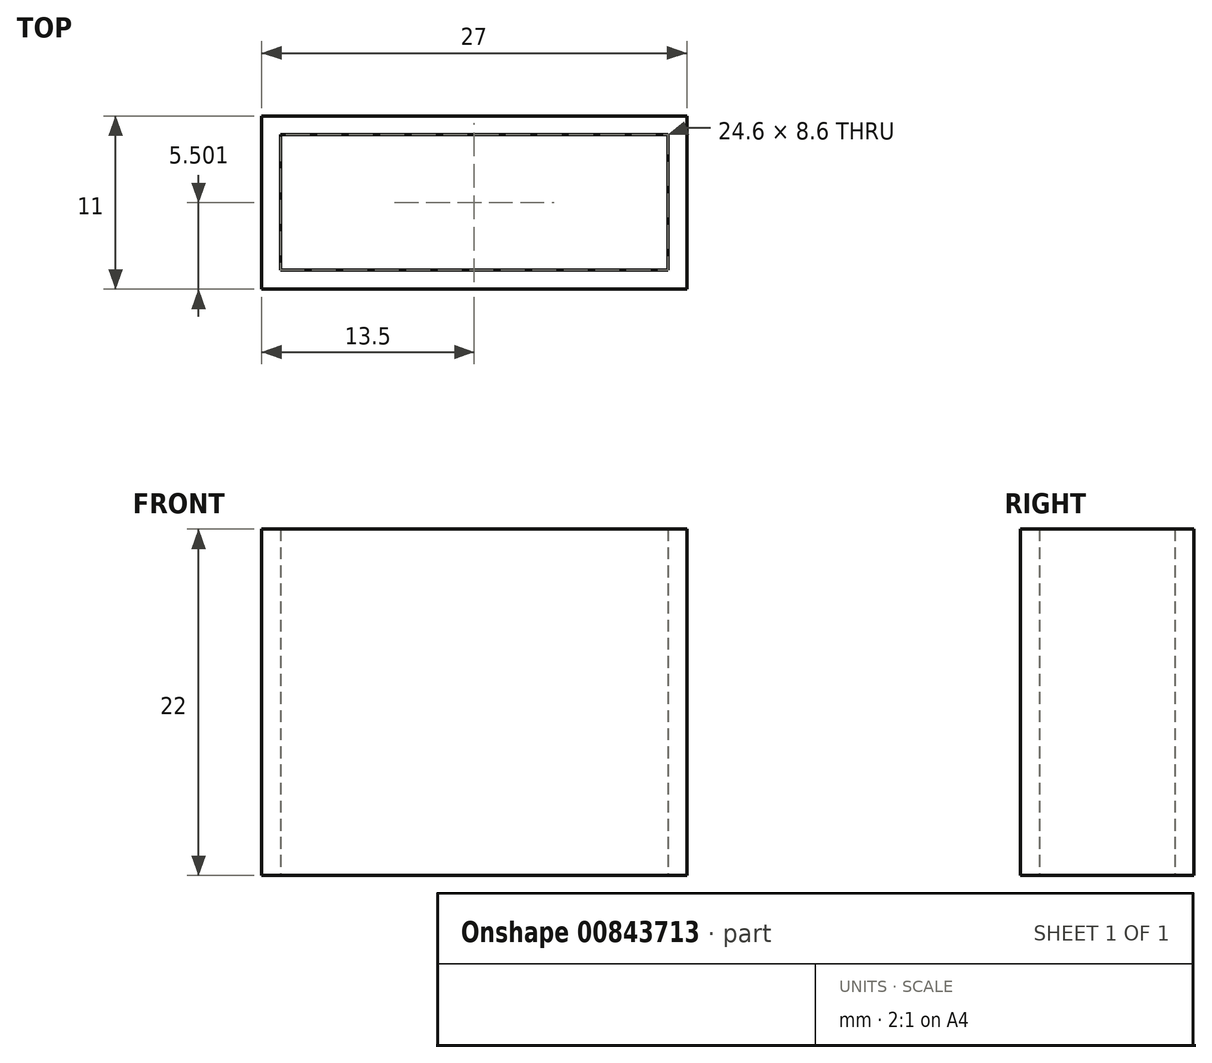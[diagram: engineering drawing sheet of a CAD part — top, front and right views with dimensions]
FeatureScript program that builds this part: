
annotation { "Feature Type Name" : "Feature", "Feature Type Description" : "" }
export const myFeature = defineFeature(function(context is Context, id is Id, definition is map)
    precondition{}
    {
        {
            var Q0;
            Q0=qCreatedBy(makeId("Top.planeOp"),FACE);
            var sketch = newSketch(context, id + "F0", { "sketchPlane" : qUnion([Q0])});
            skLineSegment(sketch, "E0.bottom", {"start": v(-13.69, 5.65) * mm, "end": v(13.31, 5.65) * mm});
            skLineSegment(sketch, "E0.top", {"start": v(-13.69, -5.35) * mm, "end": v(13.31, -5.35) * mm});
            skLineSegment(sketch, "E0.left", {"start": v(-13.69, 5.65) * mm, "end": v(-13.69, -5.35) * mm});
            skLineSegment(sketch, "E0.right", {"start": v(13.31, 5.65) * mm, "end": v(13.31, -5.35) * mm});
            skLineSegment(sketch, "E1.0", {"start": v(-12.49, 4.45) * mm, "end": v(-12.49, -4.15) * mm});
            skLineSegment(sketch, "E1.1", {"start": v(-12.49, 4.45) * mm, "end": v(12.11, 4.45) * mm});
            skLineSegment(sketch, "E1.2", {"start": v(12.11, 4.45) * mm, "end": v(12.11, -4.15) * mm});
            skLineSegment(sketch, "E1.3", {"start": v(-12.49, -4.15) * mm, "end": v(12.11, -4.15) * mm});
            skSolve(sketch);
        }
        {
            var Q0;
            Q0=makeQuery(id+"F0.imprint","IMPRINT",FACE,{"disambiguationData":[TD([[makeQuery(id+"F0.imprint","IMPRINT",EDGE,{"derivedFrom":sQuery(id+"F0.wireOp",EDGE,"E0.bottom")}),-1.0]])]});
            extrude(context, id + "F1", {"entities" : qUnion([Q0]), "depth" : 22 * mm, "offsetDistance" : 25 * mm});
        }
    });
